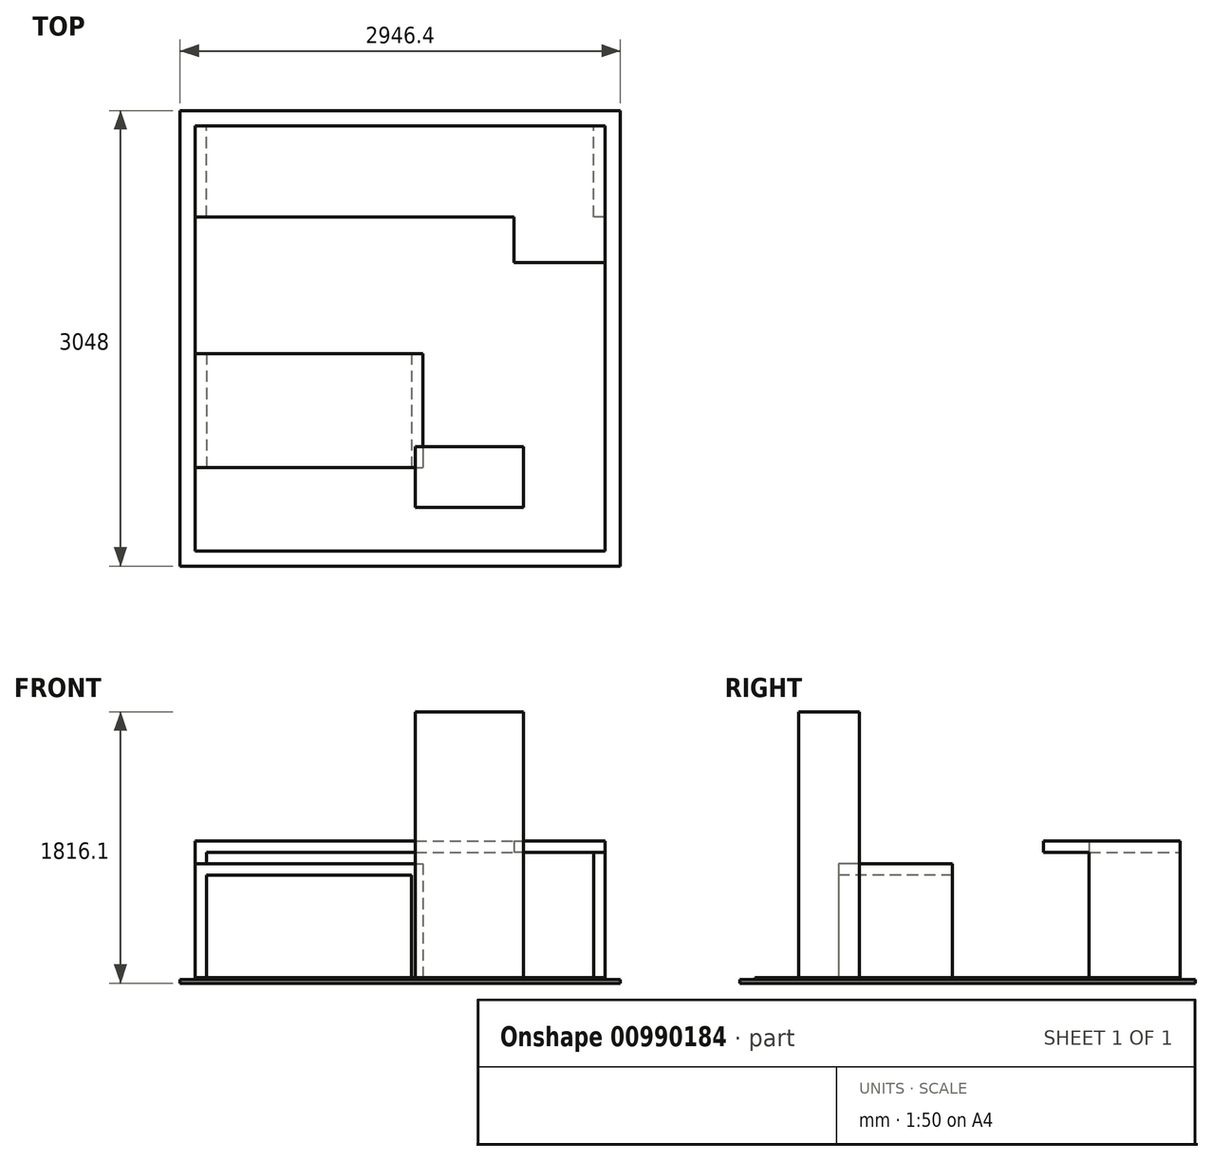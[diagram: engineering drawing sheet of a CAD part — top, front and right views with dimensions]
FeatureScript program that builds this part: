
annotation { "Feature Type Name" : "Feature", "Feature Type Description" : "" }
export const myFeature = defineFeature(function(context is Context, id is Id, definition is map)
    precondition{}
    {
        {
            var Q0;
            Q0=qCreatedBy(makeId("Top.planeOp"),FACE);
            var sketch = newSketch(context, id + "F0", { "sketchPlane" : qUnion([Q0])});
            skLineSegment(sketch, "E0.bottom", {"start": v(1473.2, 1524) * mm, "end": v(-1473.2, 1524) * mm});
            skLineSegment(sketch, "E0.top", {"start": v(1473.2, -1524) * mm, "end": v(-1473.2, -1524) * mm});
            skLineSegment(sketch, "E0.left", {"start": v(1473.2, 1524) * mm, "end": v(1473.2, -1524) * mm});
            skLineSegment(sketch, "E0.right", {"start": v(-1473.2, 1524) * mm, "end": v(-1473.2, -1524) * mm});
            skPoint(sketch, "E0.middle", {"position": v(0, 0) * mm});
            skSolve(sketch);
        }
        {
            var Q0;
            Q0=makeQuery(id+"F0.imprint","IMPRINT",FACE,{"disambiguationData":[TD([[makeQuery(id+"F0.imprint","IMPRINT",EDGE,{"derivedFrom":sQuery(id+"F0.wireOp",EDGE,"E0.bottom")}),1.0]])]});
            extrude(context, id + "F1", {"entities" : qUnion([Q0]), "depth" : 25.4 * mm, "offsetDistance" : 25.4 * mm});
        }
        {
            var Q0;
            Q0=makeQuery(id+"F1.opExtrude","CAP_FACE",FACE,{"disambiguationData":[OSD([sQuery(id+"F0.wireOp",EDGE,"E0.bottom"),sQuery(id+"F0.wireOp",EDGE,"E0.top"),sQuery(id+"F0.wireOp",EDGE,"E0.left"),sQuery(id+"F0.wireOp",EDGE,"E0.right")])],"isStart":false});
            var sketch = newSketch(context, id + "F2", { "sketchPlane" : qUnion([Q0])});
            skLineSegment(sketch, "E1.bottom", {"start": v(-1371.6, 1422.4) * mm, "end": v(1371.6, 1422.4) * mm});
            skLineSegment(sketch, "E1.top", {"start": v(-1371.6, -1422.4) * mm, "end": v(1371.6, -1422.4) * mm});
            skLineSegment(sketch, "E1.left", {"start": v(-1371.6, 1422.4) * mm, "end": v(-1371.6, -1422.4) * mm});
            skLineSegment(sketch, "E1.right", {"start": v(1371.6, 1422.4) * mm, "end": v(1371.6, -1422.4) * mm});
            skPoint(sketch, "E1.middle", {"position": v(0, 0) * mm});
            skSolve(sketch);
        }
        {
            var Q0;
            Q0 = qSketchRegion(id + "F2", true);
            extrude(context, id + "F3", {"entities" : qUnion([Q0]), "operationType" : NewBodyOperationType.ADD, "depth" : 12.7 * mm, "offsetDistance" : 25.4 * mm});
        }
        {
            var Q0;
            Q0=makeQuery(id+"F3.opExtrude","CAP_FACE",FACE,{"disambiguationData":[OSD([sQuery(id+"F2.wireOp",EDGE,"E1.bottom"),sQuery(id+"F2.wireOp",EDGE,"E1.top"),sQuery(id+"F2.wireOp",EDGE,"E1.left"),sQuery(id+"F2.wireOp",EDGE,"E1.right")])],"isStart":false});
            var sketch = newSketch(context, id + "F4", { "sketchPlane" : qUnion([Q0])});
            skLineSegment(sketch, "E2.bottom", {"start": v(-1371.6, -101.6) * mm, "end": v(152.4, -101.6) * mm});
            skLineSegment(sketch, "E2.top", {"start": v(-1371.6, -863.6) * mm, "end": v(152.4, -863.6) * mm});
            skLineSegment(sketch, "E2.left", {"start": v(-1371.6, -101.6) * mm, "end": v(-1371.6, -863.6) * mm});
            skLineSegment(sketch, "E2.right", {"start": v(152.4, -101.6) * mm, "end": v(152.4, -863.6) * mm});
            skSolve(sketch);
        }
        {
            var Q0;
            Q0 = qSketchRegion(id + "F4", true);
            extrude(context, id + "F5", {"entities" : qUnion([Q0]), "depth" : 762 * mm, "offsetDistance" : 25.4 * mm});
        }
        {
            var Q0;
            Q0=makeQuery(id+"F5.opExtrude","SWEPT_FACE",FACE,{"disambiguationData":[OSD([sQuery(id+"F4.wireOp",EDGE,"E2.top")])]});
            var sketch = newSketch(context, id + "F6", { "sketchPlane" : qUnion([Q0])});
            skLineSegment(sketch, "E3.bottom", {"start": v(-1295.4, 723.9) * mm, "end": v(76.2, 723.9) * mm});
            skLineSegment(sketch, "E3.top", {"start": v(-1295.4, 38.1) * mm, "end": v(76.2, 38.1) * mm});
            skLineSegment(sketch, "E3.left", {"start": v(-1295.4, 723.9) * mm, "end": v(-1295.4, 38.1) * mm});
            skLineSegment(sketch, "E3.right", {"start": v(76.2, 723.9) * mm, "end": v(76.2, 38.1) * mm});
            skSolve(sketch);
        }
        {
            var Q0;
            Q0=makeQuery(id+"F6.imprint","IMPRINT",FACE,{"disambiguationData":[TD([[makeQuery(id+"F6.imprint","IMPRINT",EDGE,{"derivedFrom":sQuery(id+"F6.wireOp",EDGE,"E3.bottom")}),-1.0]])]});
            extrude(context, id + "F7", {"entities" : qUnion([Q0]), "operationType" : NewBodyOperationType.REMOVE, "endBound" : BoundingType.UP_TO_NEXT, "oppositeDirection" : true, "depth" : 25.4 * mm, "offsetDistance" : 25.4 * mm});
        }
        {
            var Q0;
            Q0=makeQuery(id+"F3.opExtrude","CAP_FACE",FACE,{"disambiguationData":[OSD([sQuery(id+"F2.wireOp",EDGE,"E1.bottom"),sQuery(id+"F2.wireOp",EDGE,"E1.top"),sQuery(id+"F2.wireOp",EDGE,"E1.left"),sQuery(id+"F2.wireOp",EDGE,"E1.right")])],"isStart":false});
            var sketch = newSketch(context, id + "F8", { "sketchPlane" : qUnion([Q0])});
            skLineSegment(sketch, "E4.bottom", {"start": v(-1371.6, 1422.4) * mm, "end": v(1371.6, 1422.4) * mm});
            skLineSegment(sketch, "E4.top", {"start": v(-1371.6, 812.8) * mm, "end": v(1371.6, 812.8) * mm});
            skLineSegment(sketch, "E4.left", {"start": v(-1371.6, 1422.4) * mm, "end": v(-1371.6, 812.8) * mm});
            skLineSegment(sketch, "E4.right", {"start": v(1371.6, 1422.4) * mm, "end": v(1371.6, 812.8) * mm});
            skSolve(sketch);
        }
        {
            var Q0;
            Q0 = qSketchRegion(id + "F8", true);
            extrude(context, id + "F9", {"entities" : qUnion([Q0]), "depth" : 914.4 * mm, "offsetDistance" : 25.4 * mm});
        }
        {
            var Q0;
            Q0=makeQuery(id+"F9.opExtrude","SWEPT_FACE",FACE,{"disambiguationData":[OSD([sQuery(id+"F8.wireOp",EDGE,"E4.bottom")])]});
            var sketch = newSketch(context, id + "F10", { "sketchPlane" : qUnion([Q0])});
            skLineSegment(sketch, "E5.bottom", {"start": v(-1295.4, 876.3) * mm, "end": v(1295.4, 876.3) * mm});
            skLineSegment(sketch, "E5.top", {"start": v(-1295.4, 38.1) * mm, "end": v(1295.4, 38.1) * mm});
            skLineSegment(sketch, "E5.left", {"start": v(-1295.4, 876.3) * mm, "end": v(-1295.4, 38.1) * mm});
            skLineSegment(sketch, "E5.right", {"start": v(1295.4, 876.3) * mm, "end": v(1295.4, 38.1) * mm});
            skSolve(sketch);
        }
        {
            var Q0;
            Q0 = qSketchRegion(id + "F10", true);
            extrude(context, id + "F11", {"entities" : qUnion([Q0]), "operationType" : NewBodyOperationType.REMOVE, "endBound" : BoundingType.UP_TO_NEXT, "oppositeDirection" : true, "depth" : 25.4 * mm, "offsetDistance" : 25.4 * mm});
        }
        {
            var Q0;
            Q0=makeQuery(id+"F3.opExtrude","CAP_FACE",FACE,{"disambiguationData":[OSD([sQuery(id+"F2.wireOp",EDGE,"E1.bottom"),sQuery(id+"F2.wireOp",EDGE,"E1.top"),sQuery(id+"F2.wireOp",EDGE,"E1.left"),sQuery(id+"F2.wireOp",EDGE,"E1.right")])],"isStart":false});
            var sketch = newSketch(context, id + "F12", { "sketchPlane" : qUnion([Q0])});
            skLineSegment(sketch, "E6.bottom", {"start": v(101.35, -725.53) * mm, "end": v(825.25, -725.53) * mm});
            skLineSegment(sketch, "E6.top", {"start": v(101.35, -1131.93) * mm, "end": v(825.25, -1131.93) * mm});
            skLineSegment(sketch, "E6.left", {"start": v(101.35, -725.53) * mm, "end": v(101.35, -1131.93) * mm});
            skLineSegment(sketch, "E6.right", {"start": v(825.25, -725.53) * mm, "end": v(825.25, -1131.93) * mm});
            skSolve(sketch);
        }
        {
            var Q0;
            Q0 = qSketchRegion(id + "F12", true);
            extrude(context, id + "F13", {"entities" : qUnion([Q0]), "depth" : 1778 * mm, "offsetDistance" : 25.4 * mm});
        }
        {
            var Q0;
            Q0=makeQuery(id+"F9.opExtrude","SWEPT_FACE",FACE,{"disambiguationData":[OSD([sQuery(id+"F8.wireOp",EDGE,"E4.top")])]});
            var sketch = newSketch(context, id + "F14", { "sketchPlane" : qUnion([Q0])});
            skLineSegment(sketch, "E7.bottom", {"start": v(1371.6, 952.5) * mm, "end": v(762, 952.5) * mm});
            skLineSegment(sketch, "E7.top", {"start": v(1371.6, 876.3) * mm, "end": v(762, 876.3) * mm});
            skLineSegment(sketch, "E7.left", {"start": v(1371.6, 952.5) * mm, "end": v(1371.6, 876.3) * mm});
            skLineSegment(sketch, "E7.right", {"start": v(762, 952.5) * mm, "end": v(762, 876.3) * mm});
            skSolve(sketch);
        }
        {
            var Q0;
            Q0 = qSketchRegion(id + "F14", true);
            extrude(context, id + "F15", {"entities" : qUnion([Q0]), "operationType" : NewBodyOperationType.ADD, "depth" : 304.8 * mm, "offsetDistance" : 25.4 * mm});
        }
    });
